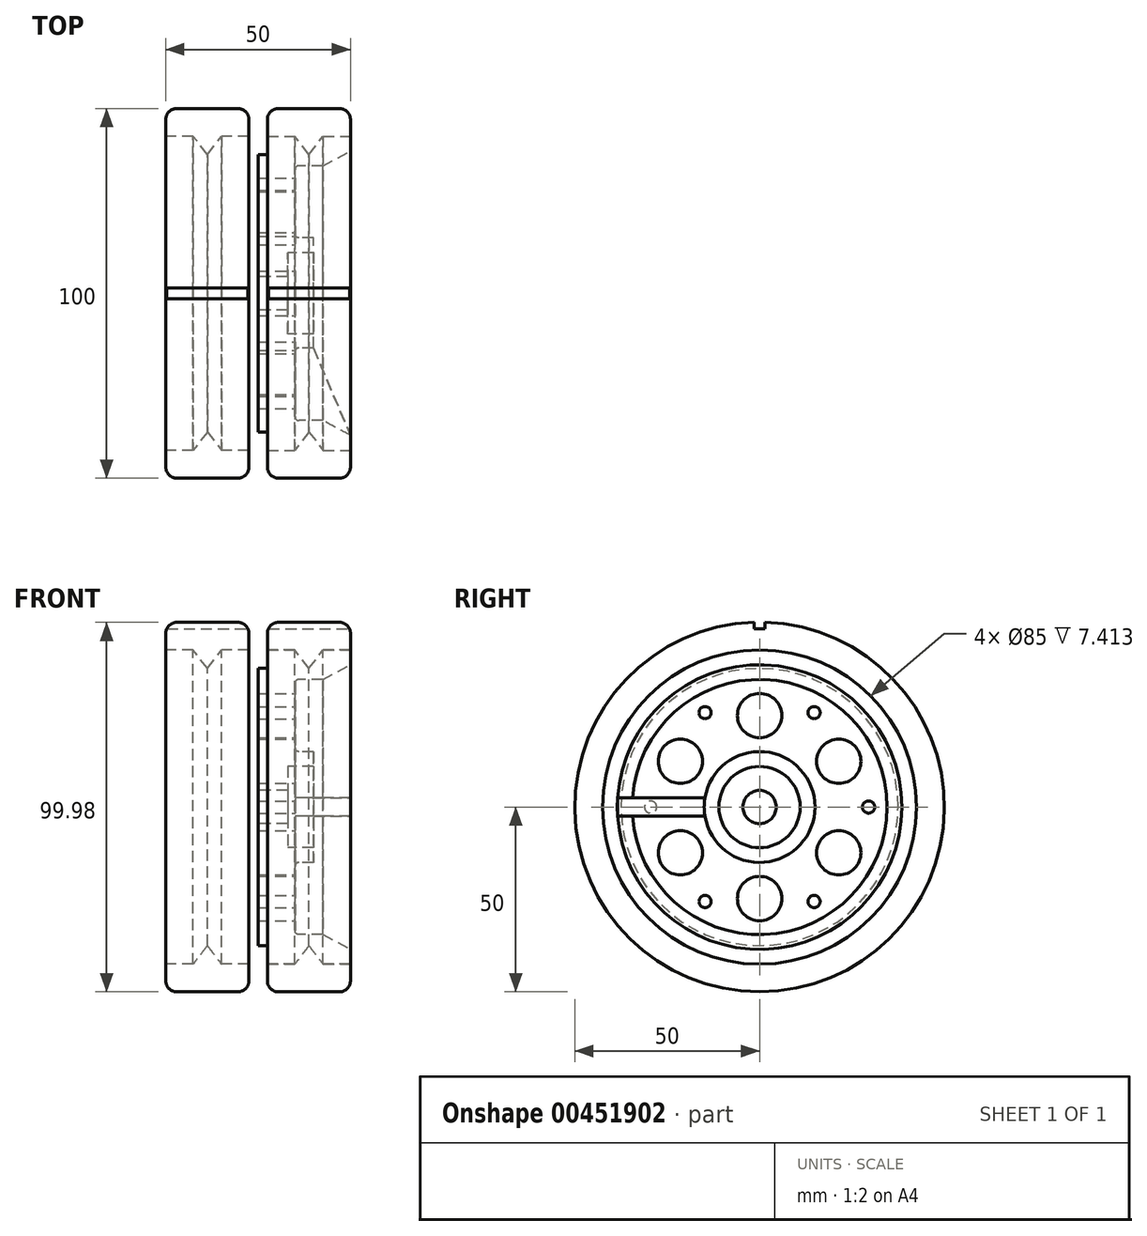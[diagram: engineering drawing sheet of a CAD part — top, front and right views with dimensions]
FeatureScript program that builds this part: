
annotation { "Feature Type Name" : "Feature", "Feature Type Description" : "" }
export const myFeature = defineFeature(function(context is Context, id is Id, definition is map)
    precondition{}
    {
        {
            var Q0;
            Q0=qCreatedBy(makeId("Front.planeOp"),FACE);
            var sketch = newSketch(context, id + "F0", { "sketchPlane" : qUnion([Q0])});
            skLineSegment(sketch, "E0", {"start": v(0, -9.53) * mm, "end": v(0, 22.6) * mm, "construction": true});
            skLineSegment(sketch, "E1", {"start": v(0, 4.5) * mm, "end": v(8, 4.5) * mm});
            skLineSegment(sketch, "E2", {"start": v(8, 4.5) * mm, "end": v(8, 11) * mm});
            skLineSegment(sketch, "E3", {"start": v(8, 11) * mm, "end": v(15, 11) * mm});
            skLineSegment(sketch, "E4", {"start": v(15, 11) * mm, "end": v(15, 15) * mm});
            skLineSegment(sketch, "E5", {"start": v(15, 15) * mm, "end": v(10, 15) * mm});
            skLineSegment(sketch, "E6", {"start": v(10, 15) * mm, "end": v(10, 34.5) * mm});
            skLineSegment(sketch, "E7", {"start": v(10, 34.5) * mm, "end": v(17.5, 34.5) * mm});
            skLineSegment(sketch, "E8", {"start": v(25, 38.5) * mm, "end": v(25, 42.5) * mm});
            skLineSegment(sketch, "E9", {"start": v(25, 42.5) * mm, "end": v(2.5, 42.5) * mm});
            skLineSegment(sketch, "E10", {"start": v(2.5, 42.5) * mm, "end": v(2.5, 37.5) * mm});
            skLineSegment(sketch, "E11", {"start": v(2.5, 37.5) * mm, "end": v(0, 37.5) * mm});
            skLineSegment(sketch, "E12", {"start": v(0, 37.5) * mm, "end": v(0, 4.5) * mm});
            skLineSegment(sketch, "E13", {"start": v(-18.36, 0) * mm, "end": v(12.99, 0) * mm, "construction": true});
            skLineSegment(sketch, "E14", {"start": v(17.5, 34.5) * mm, "end": v(25, 38.5) * mm});
            skPoint(sketch, "E15.orphan", {"position": v(25, 34.5) * mm});
            skSolve(sketch);
        }
        {
            var Q0;
            Q0=makeQuery(id+"FmgyBypNyxviDE3_0.1.F0.imprint","IMPRINT",FACE,{"disambiguationData":[TD([[makeQuery(id+"FmgyBypNyxviDE3_0.1.F0.imprint","IMPRINT",EDGE,{"derivedFrom":sQuery(id+"FmgyBypNyxviDE3_0.1.F0.wireOp",EDGE,"E1")}),1.0]])]});
            var Q1;
            Q1=makeQuery(id+"F0.imprint","IMPRINT",FACE,{"disambiguationData":[TD([[makeQuery(id+"F0.imprint","IMPRINT",EDGE,{"derivedFrom":sQuery(id+"F0.wireOp",EDGE,"E1")}),1.0]])]});
            var Q2;
            Q2=sQuery(id+"F0.wireOp",EDGE,"E13");
            revolve(context, id + "F1", {"entities" : qUnion([Q0, Q1]), "axis" : qUnion([Q2]), "revolveType" : RevolveType.FULL});
        }
        {
            var Q0;
            Q0=qCreatedBy(makeId("Front.planeOp"),FACE);
            var sketch = newSketch(context, id + "F2", { "sketchPlane" : qUnion([Q0])});
            skLineSegment(sketch, "E16", {"start": v(2.5, 42.5) * mm, "end": v(2.5, 47) * mm});
            skLineSegment(sketch, "E17", {"start": v(2.5, 42.5) * mm, "end": v(9.91, 42.5) * mm});
            skLineSegment(sketch, "E18", {"start": v(9.91, 42.5) * mm, "end": v(13.75, 37.5) * mm});
            skLineSegment(sketch, "E19", {"start": v(13.75, 37.5) * mm, "end": v(17.59, 42.5) * mm});
            skLineSegment(sketch, "E20", {"start": v(17.59, 42.5) * mm, "end": v(25, 42.5) * mm});
            skLineSegment(sketch, "E21", {"start": v(25, 42.5) * mm, "end": v(25, 47) * mm});
            skArc(sketch, "E22", {"start": v(2.5, 47) * mm, "mid": v(3.38, 49.12) * mm, "end": v(5.5, 50) * mm});
            skArc(sketch, "E23", {"start": v(25, 47) * mm, "mid": v(24.12, 49.12) * mm, "end": v(22, 50) * mm});
            skLineSegment(sketch, "E24", {"start": v(5.5, 50) * mm, "end": v(22, 50) * mm});
            skLineSegment(sketch, "E25", {"start": v(13.75, 37.5) * mm, "end": v(13.75, 42.5) * mm, "construction": true});
            skSolve(sketch);
        }
        {
            var Q0;
            Q0=makeQuery(id+"F2.imprint","IMPRINT",FACE,{"disambiguationData":[TD([[makeQuery(id+"F2.imprint","IMPRINT",EDGE,{"derivedFrom":sQuery(id+"F2.wireOp",EDGE,"E16")}),-1.0]])]});
            var Q1;
            Q1=makeQuery(id+"F1.opRevolve","SWEPT_EDGE",EDGE,{"disambiguationData":[OSD([sQuery(id+"F0.wireOp",EDGE,"E3"),sQuery(id+"F0.wireOp",EDGE,"E4")])]});
            revolve(context, id + "F3", {"entities" : qUnion([Q0]), "axis" : qUnion([Q1]), "revolveType" : RevolveType.FULL});
        }
        {
            var Q0;
            Q0=makeQuery(id+"F3.opRevolve","SWEPT_BODY",BODY,{"disambiguationData":[OSD([sQuery(id+"F2.wireOp",EDGE,"E16"),sQuery(id+"F2.wireOp",EDGE,"E17"),sQuery(id+"F2.wireOp",EDGE,"E18"),sQuery(id+"F2.wireOp",EDGE,"E19"),sQuery(id+"F2.wireOp",EDGE,"E20"),sQuery(id+"F2.wireOp",EDGE,"E21"),sQuery(id+"F2.wireOp",EDGE,"E22"),sQuery(id+"F2.wireOp",EDGE,"E23"),sQuery(id+"F2.wireOp",EDGE,"E24")])]});
            var Q1;
            Q1=qCreatedBy(makeId("Right.planeOp"),FACE);
            mirror(context, id + "F4", {"entities" : qUnion([Q0]), "mirrorPlane" : qUnion([Q1])});
        }
        {
            var Q0;
            Q0=makeQuery(id+"F1.opRevolve","SWEPT_FACE",FACE,{"disambiguationData":[OSD([sQuery(id+"F0.wireOp",EDGE,"E6")])]});
            var sketch = newSketch(context, id + "F5", { "sketchPlane" : qUnion([Q0])});
            skCircle(sketch, "E26", {"center": v(0, 0) * mm, "radius": 24.75 * mm, "construction": true});
            skCircle(sketch, "E27", {"center": v(0, 24.75) * mm, "radius": 6 * mm});
            skLineSegment(sketch, "E28", {"start": v(-15, 0) * mm, "end": v(-34.5, 0) * mm, "construction": true});
            skPoint(sketch, "E29", {"position": v(-24.75, 0) * mm});
            skCircle(sketch, "E30.1.0", {"center": v(-21.43, 12.38) * mm, "radius": 6 * mm});
            skCircle(sketch, "E30.2.0", {"center": v(-21.43, -12.37) * mm, "radius": 6 * mm});
            skCircle(sketch, "E30.3.0", {"center": v(0, -24.75) * mm, "radius": 6 * mm});
            skCircle(sketch, "E30.4.0", {"center": v(21.43, -12.38) * mm, "radius": 6 * mm});
            skCircle(sketch, "E30.5.0", {"center": v(21.43, 12.38) * mm, "radius": 6 * mm});
            skLineSegment(sketch, "E31", {"start": v(0, 0) * mm, "end": v(-12.38, -21.43) * mm, "construction": true});
            skLineSegment(sketch, "E32", {"start": v(0, 0) * mm, "end": v(12.38, -21.43) * mm, "construction": true});
            skLineSegment(sketch, "E33", {"start": v(0, 0) * mm, "end": v(12.38, 21.43) * mm, "construction": true});
            skLineSegment(sketch, "E34", {"start": v(0, 0) * mm, "end": v(-12.38, 21.43) * mm, "construction": true});
            skPoint(sketch, "E35", {"position": v(-14.75, -25.55) * mm});
            skPoint(sketch, "E36", {"position": v(14.75, -25.55) * mm});
            skPoint(sketch, "E37", {"position": v(29.5, 0) * mm});
            skPoint(sketch, "E38", {"position": v(14.75, 25.55) * mm});
            skPoint(sketch, "E39", {"position": v(-14.75, 25.55) * mm});
            skPoint(sketch, "E40", {"position": v(-29.5, 0) * mm});
            skCircle(sketch, "E41", {"center": v(0, 0) * mm, "radius": 29.5 * mm, "construction": true});
            skSolve(sketch);
        }
        {
            var Q0;
            Q0 = qSketchRegion(id + "F5", true);
            extrude(context, id + "F6", {"entities" : qUnion([Q0]), "operationType" : NewBodyOperationType.REMOVE, "oppositeDirection" : true, "depth" : 25 * mm, "offsetDistance" : 25 * mm});
        }
        {
            var Q0;
            Q0=sQuery(id+"F5.wireOp",VERTEX,"E40");
            var Q1;
            Q1=sQuery(id+"F5.wireOp",VERTEX,"E39");
            var Q2;
            Q2=sQuery(id+"F5.wireOp",VERTEX,"E38");
            var Q3;
            Q3=sQuery(id+"F5.wireOp",VERTEX,"E37");
            var Q4;
            Q4=sQuery(id+"F5.wireOp",VERTEX,"E36");
            var Q5;
            Q5=sQuery(id+"F5.wireOp",VERTEX,"E35");
            var Q6;
            Q6=makeQuery(id+"F1.opRevolve","SWEPT_BODY",BODY,{"disambiguationData":[OSD([sQuery(id+"F0.wireOp",EDGE,"E1"),sQuery(id+"F0.wireOp",EDGE,"E2"),sQuery(id+"F0.wireOp",EDGE,"E3"),sQuery(id+"F0.wireOp",EDGE,"E4"),sQuery(id+"F0.wireOp",EDGE,"E5"),sQuery(id+"F0.wireOp",EDGE,"E6"),sQuery(id+"F0.wireOp",EDGE,"E7"),sQuery(id+"F0.wireOp",EDGE,"E8"),sQuery(id+"F0.wireOp",EDGE,"E9"),sQuery(id+"F0.wireOp",EDGE,"E10"),sQuery(id+"F0.wireOp",EDGE,"E11"),sQuery(id+"F0.wireOp",EDGE,"E12"),sQuery(id+"F0.wireOp",EDGE,"E14")])]});
            var Q7;
            Q7=makeQuery(id+"F1.opRevolve","SWEPT_BODY",BODY,{"disambiguationData":[OSD([sQuery(id+"FmgyBypNyxviDE3_0.1.F0.wireOp",EDGE,"E1"),sQuery(id+"FmgyBypNyxviDE3_0.1.F0.wireOp",EDGE,"E2"),sQuery(id+"FmgyBypNyxviDE3_0.1.F0.wireOp",EDGE,"E3"),sQuery(id+"FmgyBypNyxviDE3_0.1.F0.wireOp",EDGE,"E4"),sQuery(id+"FmgyBypNyxviDE3_0.1.F0.wireOp",EDGE,"E5"),sQuery(id+"FmgyBypNyxviDE3_0.1.F0.wireOp",EDGE,"E6"),sQuery(id+"FmgyBypNyxviDE3_0.1.F0.wireOp",EDGE,"E7"),sQuery(id+"FmgyBypNyxviDE3_0.1.F0.wireOp",EDGE,"E8"),sQuery(id+"FmgyBypNyxviDE3_0.1.F0.wireOp",EDGE,"E9"),sQuery(id+"FmgyBypNyxviDE3_0.1.F0.wireOp",EDGE,"E10"),sQuery(id+"FmgyBypNyxviDE3_0.1.F0.wireOp",EDGE,"E11"),sQuery(id+"FmgyBypNyxviDE3_0.1.F0.wireOp",EDGE,"E12"),sQuery(id+"FmgyBypNyxviDE3_0.1.F0.wireOp",EDGE,"E14")])]});
            hole(context, id + "F7", {"style" : HoleStyle.SIMPLE, "endStyle" : HoleEndStyle.THROUGH, "standardTappedOrClearance" : lookupTablePath({ "standard" : "ISO", "fit" : "Normal", "size" : "M3", "type" : "Clearance" }), "standardBlindInLast" : lookupTablePath({ "fit" : "Standard", "standard" : "ISO", "size" : "M3", "type" : "Clearance" }), "holeDiameter" : 3.3 * mm, "tappedDepth" : 12 * mm, "tapClearance" : 3, "locations" : qUnion([Q0, Q1, Q2, Q3, Q4, Q5]), "scope" : qUnion([Q6, Q7])});
        }
        {
            var Q0;
            Q0=qCreatedBy(makeId("Right.planeOp"),FACE);
            var sketch = newSketch(context, id + "F8", { "sketchPlane" : qUnion([Q0])});
            skLineSegment(sketch, "E42.bottom", {"start": v(1.5, 48.25) * mm, "end": v(-1.5, 48.25) * mm});
            skLineSegment(sketch, "E42.top", {"start": v(1.5, 51.75) * mm, "end": v(-1.5, 51.75) * mm});
            skLineSegment(sketch, "E42.left", {"start": v(1.5, 48.25) * mm, "end": v(1.5, 51.75) * mm});
            skLineSegment(sketch, "E42.right", {"start": v(-1.5, 48.25) * mm, "end": v(-1.5, 51.75) * mm});
            skPoint(sketch, "E42.middle", {"position": v(0, 50) * mm});
            skCircle(sketch, "E43.0", {"center": v(0, 0) * mm, "radius": 50 * mm, "construction": true});
            skSolve(sketch);
        }
        {
            var Q0;
            Q0 = qSketchRegion(id + "F8", true);
            extrude(context, id + "F9", {"entities" : qUnion([Q0]), "operationType" : NewBodyOperationType.REMOVE, "endBound" : BoundingType.SYMMETRIC, "oppositeDirection" : true, "depth" : 100 * mm, "offsetDistance" : 25 * mm});
        }
        {
            var Q0;
            Q0=makeQuery(id+"F1.opRevolve","SWEPT_FACE",FACE,{"disambiguationData":[OSD([sQuery(id+"F0.wireOp",EDGE,"E4")])]});
            var sketch = newSketch(context, id + "F10", { "sketchPlane" : qUnion([Q0])});
            skArc(sketch, "E44", {"start": v(-14.8, 2.5) * mm, "mid": v(-15, 0) * mm, "end": v(-14.8, -2.5) * mm});
            skArc(sketch, "E45", {"start": v(-14.8, -2.5) * mm, "mid": v(15, 0) * mm, "end": v(-14.8, 2.5) * mm});
            skSolve(sketch);
        }
        {
            var Q0;
            Q0=qCreatedBy(makeId("Top.planeOp"),FACE);
            var Q1;
            Q1=sQuery(id+"F10.wireOp",VERTEX,"E44.start");
            cPlane(context, id + "F11", {"entities" : qUnion([Q0, Q1]), "cplaneType" : CPlaneType.PLANE_POINT, "offset" : 25 * mm, "width" : 150 * mm, "height" : 150 * mm});
        }
        {
            var Q0;
            Q0=qCreatedBy(id+"F11.planeOp",FACE);
            var sketch = newSketch(context, id + "F12", { "sketchPlane" : qUnion([Q0])});
            skLineSegment(sketch, "E46", {"start": v(15, -14.8) * mm, "end": v(10, -14.8) * mm});
            skLineSegment(sketch, "E47", {"start": v(10, -14.8) * mm, "end": v(10, -34.4) * mm});
            skLineSegment(sketch, "E48", {"start": v(25, -38.42) * mm, "end": v(15, -14.8) * mm});
            skLineSegment(sketch, "E49", {"start": v(10, -34.4) * mm, "end": v(25, -38.42) * mm});
            skSolve(sketch);
        }
        {
            var Q0;
            Q0=makeQuery(id+"F12.imprint","IMPRINT",FACE,{"disambiguationData":[TD([[makeQuery(id+"F12.imprint","IMPRINT",EDGE,{"derivedFrom":sQuery(id+"F12.wireOp",EDGE,"E46")}),1.0]])]});
            var Q1;
            Q1=sQuery(id+"F10.wireOp",EDGE,"E44");
            sweep(context, id + "F13", {"operationType" : NewBodyOperationType.ADD, "profiles" : qUnion([Q0]), "path" : qUnion([Q1]), "keepProfileOrientation" : true});
        }
        {
            var Q0;
            Q0=makeQuery(id+"F1.opRevolve","SWEPT_EDGE",EDGE,{"disambiguationData":[OSD([sQuery(id+"F0.wireOp",EDGE,"E6"),sQuery(id+"F0.wireOp",EDGE,"E7")])]});
            var Q1;
            Q1=makeQuery(id+"F1.opRevolve","SWEPT_EDGE",EDGE,{"disambiguationData":[OSD([sQuery(id+"FmgyBypNyxviDE3_0.1.F0.wireOp",EDGE,"E6"),sQuery(id+"FmgyBypNyxviDE3_0.1.F0.wireOp",EDGE,"E7")])]});
            var Q2;
            {var subQ0=sQuery(id+"FmgyBypNyxviDE3_0.1.F0.wireOp",EDGE,"E5");var subQ2=sQuery(id+"FmgyBypNyxviDE3_0.1.F0.wireOp",EDGE,"E6");var subQ4=sQuery(id+"F12.wireOp",EDGE,"E48");var subQ5=sQuery(id+"F12.wireOp",EDGE,"E47");var subQ6=sQuery(id+"F12.wireOp",EDGE,"E46");var subQ7=makeQuery(id+"FEM153JQDZezefJ_4.1.F2I4MMrCVyspTrr_4.1.F13.opSweep","CAP_FACE",FACE,{"disambiguationData":[OSD([sQuery(id+"F10.wireOp",VERTEX,"E44.start"),subQ6,subQ5,subQ4])],"isStart":true});var subQ8=sQuery(id+"F10.wireOp",VERTEX,"E44.end");Q2=makeQuery(id+"FEM153JQDZezefJ_4.1.F2I4MMrCVyspTrr_4.2.F13.boolean.opBoolean","SPLIT",EDGE,{"disambiguationData":[TD([subQ7])],"derivedFrom":makeQuery(id+"FEM153JQDZezefJ_4.1.F2I4MMrCVyspTrr_4.1.F13.boolean.opBoolean","SPLIT",EDGE,{"disambiguationData":[TD([makeQuery(id+"FEM153JQDZezefJ_4.1.F13.opSweep","CAP_FACE",FACE,{"disambiguationData":[OSD([subQ8,subQ6,subQ5,subQ4])],"isStart":false})])],"derivedFrom":makeQuery(id+"F1.opRevolve","SWEPT_EDGE",EDGE,{"disambiguationData":[OSD([subQ0,subQ2])]})})});}
            var Q3;
            {var subQ0=sQuery(id+"FmgyBypNyxviDE3_0.1.F0.wireOp",EDGE,"E5");var subQ2=sQuery(id+"FmgyBypNyxviDE3_0.1.F0.wireOp",EDGE,"E6");var subQ4=sQuery(id+"F12.wireOp",EDGE,"E48");var subQ5=sQuery(id+"F12.wireOp",EDGE,"E47");var subQ6=sQuery(id+"F12.wireOp",EDGE,"E46");var subQ7=sQuery(id+"F10.wireOp",VERTEX,"E44.end");var subQ8=sQuery(id+"F10.wireOp",VERTEX,"E44.start");var subQ9=makeQuery(id+"FEM153JQDZezefJ_4.1.F2I4MMrCVyspTrr_4.2.F13.opSweep","CAP_FACE",FACE,{"disambiguationData":[OSD([subQ8,subQ6,subQ5,subQ4])],"isStart":true});var subQ10=makeQuery(id+"FEM153JQDZezefJ_4.1.F13.opSweep","CAP_FACE",FACE,{"disambiguationData":[OSD([subQ7,subQ6,subQ5,subQ4])],"isStart":false});Q3=makeQuery(id+"FEM153JQDZezefJ_4.1.F2I4MMrCVyspTrr_4.3.F13.boolean.opBoolean","SPLIT",EDGE,{"disambiguationData":[TD([subQ9])],"derivedFrom":makeQuery(id+"FEM153JQDZezefJ_4.1.F2I4MMrCVyspTrr_4.2.F13.boolean.opBoolean","SPLIT",EDGE,{"disambiguationData":[TD([subQ10])],"derivedFrom":makeQuery(id+"FEM153JQDZezefJ_4.1.F2I4MMrCVyspTrr_4.1.F13.boolean.opBoolean","SPLIT",EDGE,{"disambiguationData":[TD([subQ10])],"derivedFrom":makeQuery(id+"F1.opRevolve","SWEPT_EDGE",EDGE,{"disambiguationData":[OSD([subQ0,subQ2])]})})})});}
            var Q4;
            {var subQ0=sQuery(id+"FmgyBypNyxviDE3_0.1.F0.wireOp",EDGE,"E5");var subQ2=sQuery(id+"F12.wireOp",EDGE,"E48");var subQ3=sQuery(id+"F12.wireOp",EDGE,"E47");var subQ4=sQuery(id+"F12.wireOp",EDGE,"E46");var subQ5=sQuery(id+"F10.wireOp",VERTEX,"E44.start");var subQ6=makeQuery(id+"FEM153JQDZezefJ_4.1.F2I4MMrCVyspTrr_4.3.F13.opSweep","CAP_FACE",FACE,{"disambiguationData":[OSD([subQ5,subQ4,subQ3,subQ2])],"isStart":true});var subQ7=sQuery(id+"FmgyBypNyxviDE3_0.1.F0.wireOp",EDGE,"E6");var subQ9=sQuery(id+"F10.wireOp",VERTEX,"E44.end");var subQ10=makeQuery(id+"FEM153JQDZezefJ_4.1.F13.opSweep","CAP_FACE",FACE,{"disambiguationData":[OSD([subQ9,subQ4,subQ3,subQ2])],"isStart":false});Q4=makeQuery(id+"FEM153JQDZezefJ_4.1.F2I4MMrCVyspTrr_4.4.F13.boolean.opBoolean","SPLIT",EDGE,{"disambiguationData":[TD([subQ6])],"derivedFrom":makeQuery(id+"FEM153JQDZezefJ_4.1.F2I4MMrCVyspTrr_4.3.F13.boolean.opBoolean","SPLIT",EDGE,{"disambiguationData":[TD([subQ10])],"derivedFrom":makeQuery(id+"FEM153JQDZezefJ_4.1.F2I4MMrCVyspTrr_4.2.F13.boolean.opBoolean","SPLIT",EDGE,{"disambiguationData":[TD([subQ10])],"derivedFrom":makeQuery(id+"FEM153JQDZezefJ_4.1.F2I4MMrCVyspTrr_4.1.F13.boolean.opBoolean","SPLIT",EDGE,{"disambiguationData":[TD([subQ10])],"derivedFrom":makeQuery(id+"F1.opRevolve","SWEPT_EDGE",EDGE,{"disambiguationData":[OSD([subQ0,subQ7])]})})})})});}
            var Q5;
            {var subQ0=sQuery(id+"FmgyBypNyxviDE3_0.1.F0.wireOp",EDGE,"E5");var subQ1=sQuery(id+"F12.wireOp",EDGE,"E48");var subQ2=sQuery(id+"F12.wireOp",EDGE,"E47");var subQ3=sQuery(id+"F12.wireOp",EDGE,"E46");var subQ4=sQuery(id+"FmgyBypNyxviDE3_0.1.F0.wireOp",EDGE,"E6");Q5=makeQuery(id+"FEM153JQDZezefJ_4.1.F2I4MMrCVyspTrr_4.1.F13.boolean.opBoolean","SPLIT",EDGE,{"disambiguationData":[TD([makeQuery(id+"FEM153JQDZezefJ_4.1.F13.opSweep","CAP_FACE",FACE,{"disambiguationData":[OSD([sQuery(id+"F10.wireOp",VERTEX,"E44.start"),subQ3,subQ2,subQ1])],"isStart":true})])],"derivedFrom":makeQuery(id+"F1.opRevolve","SWEPT_EDGE",EDGE,{"disambiguationData":[OSD([subQ0,subQ4])]})});}
            var Q6;
            {var subQ0=sQuery(id+"FmgyBypNyxviDE3_0.1.F0.wireOp",EDGE,"E5");var subQ2=sQuery(id+"FmgyBypNyxviDE3_0.1.F0.wireOp",EDGE,"E6");var subQ4=sQuery(id+"F12.wireOp",EDGE,"E48");var subQ5=sQuery(id+"F12.wireOp",EDGE,"E47");var subQ6=sQuery(id+"F12.wireOp",EDGE,"E46");var subQ8=makeQuery(id+"FEM153JQDZezefJ_4.1.F13.opSweep","CAP_FACE",FACE,{"disambiguationData":[OSD([sQuery(id+"F10.wireOp",VERTEX,"E44.end"),subQ6,subQ5,subQ4])],"isStart":false});Q6=makeQuery(id+"FEM153JQDZezefJ_4.1.F2I4MMrCVyspTrr_4.5.F13.boolean.opBoolean","SPLIT",EDGE,{"disambiguationData":[TD([subQ8])],"derivedFrom":makeQuery(id+"FEM153JQDZezefJ_4.1.F2I4MMrCVyspTrr_4.4.F13.boolean.opBoolean","SPLIT",EDGE,{"disambiguationData":[TD([subQ8])],"derivedFrom":makeQuery(id+"FEM153JQDZezefJ_4.1.F2I4MMrCVyspTrr_4.3.F13.boolean.opBoolean","SPLIT",EDGE,{"disambiguationData":[TD([subQ8])],"derivedFrom":makeQuery(id+"FEM153JQDZezefJ_4.1.F2I4MMrCVyspTrr_4.2.F13.boolean.opBoolean","SPLIT",EDGE,{"disambiguationData":[TD([subQ8])],"derivedFrom":makeQuery(id+"FEM153JQDZezefJ_4.1.F2I4MMrCVyspTrr_4.1.F13.boolean.opBoolean","SPLIT",EDGE,{"disambiguationData":[TD([subQ8])],"derivedFrom":makeQuery(id+"F1.opRevolve","SWEPT_EDGE",EDGE,{"disambiguationData":[OSD([subQ0,subQ2])]})})})})})});}
            var Q7;
            {var subQ0=sQuery(id+"FmgyBypNyxviDE3_0.1.F0.wireOp",EDGE,"E5");var subQ2=sQuery(id+"FmgyBypNyxviDE3_0.1.F0.wireOp",EDGE,"E6");var subQ4=sQuery(id+"F12.wireOp",EDGE,"E48");var subQ5=sQuery(id+"F12.wireOp",EDGE,"E47");var subQ6=sQuery(id+"F12.wireOp",EDGE,"E46");var subQ7=sQuery(id+"F10.wireOp",VERTEX,"E44.start");var subQ8=makeQuery(id+"FEM153JQDZezefJ_4.1.F2I4MMrCVyspTrr_4.4.F13.opSweep","CAP_FACE",FACE,{"disambiguationData":[OSD([subQ7,subQ6,subQ5,subQ4])],"isStart":true});var subQ9=sQuery(id+"F10.wireOp",VERTEX,"E44.end");var subQ10=makeQuery(id+"FEM153JQDZezefJ_4.1.F13.opSweep","CAP_FACE",FACE,{"disambiguationData":[OSD([subQ9,subQ6,subQ5,subQ4])],"isStart":false});Q7=makeQuery(id+"FEM153JQDZezefJ_4.1.F2I4MMrCVyspTrr_4.5.F13.boolean.opBoolean","SPLIT",EDGE,{"disambiguationData":[TD([subQ8])],"derivedFrom":makeQuery(id+"FEM153JQDZezefJ_4.1.F2I4MMrCVyspTrr_4.4.F13.boolean.opBoolean","SPLIT",EDGE,{"disambiguationData":[TD([subQ10])],"derivedFrom":makeQuery(id+"FEM153JQDZezefJ_4.1.F2I4MMrCVyspTrr_4.3.F13.boolean.opBoolean","SPLIT",EDGE,{"disambiguationData":[TD([subQ10])],"derivedFrom":makeQuery(id+"FEM153JQDZezefJ_4.1.F2I4MMrCVyspTrr_4.2.F13.boolean.opBoolean","SPLIT",EDGE,{"disambiguationData":[TD([subQ10])],"derivedFrom":makeQuery(id+"FEM153JQDZezefJ_4.1.F2I4MMrCVyspTrr_4.1.F13.boolean.opBoolean","SPLIT",EDGE,{"disambiguationData":[TD([subQ10])],"derivedFrom":makeQuery(id+"F1.opRevolve","SWEPT_EDGE",EDGE,{"disambiguationData":[OSD([subQ0,subQ2])]})})})})})});}
            var Q8;
            {var subQ0=sQuery(id+"F0.wireOp",EDGE,"E5");var subQ2=sQuery(id+"F12.wireOp",EDGE,"E48");var subQ3=sQuery(id+"F12.wireOp",EDGE,"E47");var subQ4=sQuery(id+"F12.wireOp",EDGE,"E46");var subQ5=sQuery(id+"F10.wireOp",VERTEX,"E44.start");var subQ6=makeQuery(id+"F2I4MMrCVyspTrr_4.3.F13.opSweep","CAP_FACE",FACE,{"disambiguationData":[OSD([subQ5,subQ4,subQ3,subQ2])],"isStart":true});var subQ7=sQuery(id+"F0.wireOp",EDGE,"E6");var subQ9=sQuery(id+"F10.wireOp",VERTEX,"E44.end");var subQ10=makeQuery(id+"F13.opSweep","CAP_FACE",FACE,{"disambiguationData":[OSD([subQ9,subQ4,subQ3,subQ2])],"isStart":false});Q8=makeQuery(id+"F2I4MMrCVyspTrr_4.4.F13.boolean.opBoolean","SPLIT",EDGE,{"disambiguationData":[TD([subQ6])],"derivedFrom":makeQuery(id+"F2I4MMrCVyspTrr_4.3.F13.boolean.opBoolean","SPLIT",EDGE,{"disambiguationData":[TD([subQ10])],"derivedFrom":makeQuery(id+"F2I4MMrCVyspTrr_4.2.F13.boolean.opBoolean","SPLIT",EDGE,{"disambiguationData":[TD([subQ10])],"derivedFrom":makeQuery(id+"F2I4MMrCVyspTrr_4.1.F13.boolean.opBoolean","SPLIT",EDGE,{"disambiguationData":[TD([subQ10])],"derivedFrom":makeQuery(id+"F1.opRevolve","SWEPT_EDGE",EDGE,{"disambiguationData":[OSD([subQ0,subQ7])]})})})})});}
            var Q9;
            {var subQ0=sQuery(id+"F0.wireOp",EDGE,"E5");var subQ2=sQuery(id+"F0.wireOp",EDGE,"E6");var subQ4=sQuery(id+"F12.wireOp",EDGE,"E48");var subQ5=sQuery(id+"F12.wireOp",EDGE,"E47");var subQ6=sQuery(id+"F12.wireOp",EDGE,"E46");var subQ7=sQuery(id+"F10.wireOp",VERTEX,"E44.start");var subQ8=makeQuery(id+"F2I4MMrCVyspTrr_4.4.F13.opSweep","CAP_FACE",FACE,{"disambiguationData":[OSD([subQ7,subQ6,subQ5,subQ4])],"isStart":true});var subQ9=sQuery(id+"F10.wireOp",VERTEX,"E44.end");var subQ10=makeQuery(id+"F13.opSweep","CAP_FACE",FACE,{"disambiguationData":[OSD([subQ9,subQ6,subQ5,subQ4])],"isStart":false});Q9=makeQuery(id+"F2I4MMrCVyspTrr_4.5.F13.boolean.opBoolean","SPLIT",EDGE,{"disambiguationData":[TD([subQ8])],"derivedFrom":makeQuery(id+"F2I4MMrCVyspTrr_4.4.F13.boolean.opBoolean","SPLIT",EDGE,{"disambiguationData":[TD([subQ10])],"derivedFrom":makeQuery(id+"F2I4MMrCVyspTrr_4.3.F13.boolean.opBoolean","SPLIT",EDGE,{"disambiguationData":[TD([subQ10])],"derivedFrom":makeQuery(id+"F2I4MMrCVyspTrr_4.2.F13.boolean.opBoolean","SPLIT",EDGE,{"disambiguationData":[TD([subQ10])],"derivedFrom":makeQuery(id+"F2I4MMrCVyspTrr_4.1.F13.boolean.opBoolean","SPLIT",EDGE,{"disambiguationData":[TD([subQ10])],"derivedFrom":makeQuery(id+"F1.opRevolve","SWEPT_EDGE",EDGE,{"disambiguationData":[OSD([subQ0,subQ2])]})})})})})});}
            var Q10;
            {var subQ0=sQuery(id+"F0.wireOp",EDGE,"E5");var subQ2=sQuery(id+"F0.wireOp",EDGE,"E6");var subQ4=sQuery(id+"F12.wireOp",EDGE,"E48");var subQ5=sQuery(id+"F12.wireOp",EDGE,"E47");var subQ6=sQuery(id+"F12.wireOp",EDGE,"E46");var subQ7=sQuery(id+"F10.wireOp",VERTEX,"E44.end");var subQ8=sQuery(id+"F10.wireOp",VERTEX,"E44.start");var subQ9=makeQuery(id+"F2I4MMrCVyspTrr_4.2.F13.opSweep","CAP_FACE",FACE,{"disambiguationData":[OSD([subQ8,subQ6,subQ5,subQ4])],"isStart":true});var subQ10=makeQuery(id+"F13.opSweep","CAP_FACE",FACE,{"disambiguationData":[OSD([subQ7,subQ6,subQ5,subQ4])],"isStart":false});Q10=makeQuery(id+"F2I4MMrCVyspTrr_4.3.F13.boolean.opBoolean","SPLIT",EDGE,{"disambiguationData":[TD([subQ9])],"derivedFrom":makeQuery(id+"F2I4MMrCVyspTrr_4.2.F13.boolean.opBoolean","SPLIT",EDGE,{"disambiguationData":[TD([subQ10])],"derivedFrom":makeQuery(id+"F2I4MMrCVyspTrr_4.1.F13.boolean.opBoolean","SPLIT",EDGE,{"disambiguationData":[TD([subQ10])],"derivedFrom":makeQuery(id+"F1.opRevolve","SWEPT_EDGE",EDGE,{"disambiguationData":[OSD([subQ0,subQ2])]})})})});}
            var Q11;
            {var subQ0=sQuery(id+"F0.wireOp",EDGE,"E5");var subQ2=sQuery(id+"F0.wireOp",EDGE,"E6");var subQ4=sQuery(id+"F12.wireOp",EDGE,"E48");var subQ5=sQuery(id+"F12.wireOp",EDGE,"E47");var subQ6=sQuery(id+"F12.wireOp",EDGE,"E46");var subQ7=makeQuery(id+"F2I4MMrCVyspTrr_4.1.F13.opSweep","CAP_FACE",FACE,{"disambiguationData":[OSD([sQuery(id+"F10.wireOp",VERTEX,"E44.start"),subQ6,subQ5,subQ4])],"isStart":true});var subQ8=sQuery(id+"F10.wireOp",VERTEX,"E44.end");Q11=makeQuery(id+"F2I4MMrCVyspTrr_4.2.F13.boolean.opBoolean","SPLIT",EDGE,{"disambiguationData":[TD([subQ7])],"derivedFrom":makeQuery(id+"F2I4MMrCVyspTrr_4.1.F13.boolean.opBoolean","SPLIT",EDGE,{"disambiguationData":[TD([makeQuery(id+"F13.opSweep","CAP_FACE",FACE,{"disambiguationData":[OSD([subQ8,subQ6,subQ5,subQ4])],"isStart":false})])],"derivedFrom":makeQuery(id+"F1.opRevolve","SWEPT_EDGE",EDGE,{"disambiguationData":[OSD([subQ0,subQ2])]})})});}
            var Q12;
            {var subQ0=sQuery(id+"F0.wireOp",EDGE,"E5");var subQ1=sQuery(id+"F12.wireOp",EDGE,"E48");var subQ2=sQuery(id+"F12.wireOp",EDGE,"E47");var subQ3=sQuery(id+"F12.wireOp",EDGE,"E46");var subQ4=sQuery(id+"F0.wireOp",EDGE,"E6");Q12=makeQuery(id+"F2I4MMrCVyspTrr_4.1.F13.boolean.opBoolean","SPLIT",EDGE,{"disambiguationData":[TD([makeQuery(id+"F13.opSweep","CAP_FACE",FACE,{"disambiguationData":[OSD([sQuery(id+"F10.wireOp",VERTEX,"E44.start"),subQ3,subQ2,subQ1])],"isStart":true})])],"derivedFrom":makeQuery(id+"F1.opRevolve","SWEPT_EDGE",EDGE,{"disambiguationData":[OSD([subQ0,subQ4])]})});}
            var Q13;
            {var subQ0=sQuery(id+"F0.wireOp",EDGE,"E5");var subQ2=sQuery(id+"F0.wireOp",EDGE,"E6");var subQ4=sQuery(id+"F12.wireOp",EDGE,"E48");var subQ5=sQuery(id+"F12.wireOp",EDGE,"E47");var subQ6=sQuery(id+"F12.wireOp",EDGE,"E46");var subQ8=makeQuery(id+"F13.opSweep","CAP_FACE",FACE,{"disambiguationData":[OSD([sQuery(id+"F10.wireOp",VERTEX,"E44.end"),subQ6,subQ5,subQ4])],"isStart":false});Q13=makeQuery(id+"F2I4MMrCVyspTrr_4.5.F13.boolean.opBoolean","SPLIT",EDGE,{"disambiguationData":[TD([subQ8])],"derivedFrom":makeQuery(id+"F2I4MMrCVyspTrr_4.4.F13.boolean.opBoolean","SPLIT",EDGE,{"disambiguationData":[TD([subQ8])],"derivedFrom":makeQuery(id+"F2I4MMrCVyspTrr_4.3.F13.boolean.opBoolean","SPLIT",EDGE,{"disambiguationData":[TD([subQ8])],"derivedFrom":makeQuery(id+"F2I4MMrCVyspTrr_4.2.F13.boolean.opBoolean","SPLIT",EDGE,{"disambiguationData":[TD([subQ8])],"derivedFrom":makeQuery(id+"F2I4MMrCVyspTrr_4.1.F13.boolean.opBoolean","SPLIT",EDGE,{"disambiguationData":[TD([subQ8])],"derivedFrom":makeQuery(id+"F1.opRevolve","SWEPT_EDGE",EDGE,{"disambiguationData":[OSD([subQ0,subQ2])]})})})})})});}
            fillet(context, id + "F14", {"entities" : qUnion([Q0, Q1, Q2, Q3, Q4, Q5, Q6, Q7, Q8, Q9, Q10, Q11, Q12, Q13]), "radius" : 1 * mm, "tangentPropagation" : true, "allowEdgeOverflow" : false});
        }
        {
            var Q0;
            Q0=makeQuery(id+"F3.opRevolve","SWEPT_BODY",BODY,{"disambiguationData":[OSD([sQuery(id+"F2.wireOp",EDGE,"E16"),sQuery(id+"F2.wireOp",EDGE,"E17"),sQuery(id+"F2.wireOp",EDGE,"E18"),sQuery(id+"F2.wireOp",EDGE,"E19"),sQuery(id+"F2.wireOp",EDGE,"E20"),sQuery(id+"F2.wireOp",EDGE,"E21"),sQuery(id+"F2.wireOp",EDGE,"E22"),sQuery(id+"F2.wireOp",EDGE,"E23"),sQuery(id+"F2.wireOp",EDGE,"E24")])]});
            var Q1;
            Q1=makeQuery(id+"F4.opPattern","COPY",BODY,{"derivedFrom":makeQuery(id+"F3.opRevolve","SWEPT_BODY",BODY,{"disambiguationData":[OSD([sQuery(id+"F2.wireOp",EDGE,"E16"),sQuery(id+"F2.wireOp",EDGE,"E17"),sQuery(id+"F2.wireOp",EDGE,"E18"),sQuery(id+"F2.wireOp",EDGE,"E19"),sQuery(id+"F2.wireOp",EDGE,"E20"),sQuery(id+"F2.wireOp",EDGE,"E21"),sQuery(id+"F2.wireOp",EDGE,"E22"),sQuery(id+"F2.wireOp",EDGE,"E23"),sQuery(id+"F2.wireOp",EDGE,"E24")])]}),"instanceName":"1"});
            var Q2;
            Q2=makeQuery(id+"F1.opRevolve","SWEPT_BODY",BODY,{"disambiguationData":[OSD([sQuery(id+"FmgyBypNyxviDE3_0.1.F0.wireOp",EDGE,"E1"),sQuery(id+"FmgyBypNyxviDE3_0.1.F0.wireOp",EDGE,"E2"),sQuery(id+"FmgyBypNyxviDE3_0.1.F0.wireOp",EDGE,"E3"),sQuery(id+"FmgyBypNyxviDE3_0.1.F0.wireOp",EDGE,"E4"),sQuery(id+"FmgyBypNyxviDE3_0.1.F0.wireOp",EDGE,"E5"),sQuery(id+"FmgyBypNyxviDE3_0.1.F0.wireOp",EDGE,"E6"),sQuery(id+"FmgyBypNyxviDE3_0.1.F0.wireOp",EDGE,"E7"),sQuery(id+"FmgyBypNyxviDE3_0.1.F0.wireOp",EDGE,"E8"),sQuery(id+"FmgyBypNyxviDE3_0.1.F0.wireOp",EDGE,"E9"),sQuery(id+"FmgyBypNyxviDE3_0.1.F0.wireOp",EDGE,"E10"),sQuery(id+"FmgyBypNyxviDE3_0.1.F0.wireOp",EDGE,"E11"),sQuery(id+"FmgyBypNyxviDE3_0.1.F0.wireOp",EDGE,"E12"),sQuery(id+"FmgyBypNyxviDE3_0.1.F0.wireOp",EDGE,"E14")])]});
            var Q3;
            Q3=makeQuery(id+"F1.opRevolve","SWEPT_BODY",BODY,{"disambiguationData":[OSD([sQuery(id+"F0.wireOp",EDGE,"E1"),sQuery(id+"F0.wireOp",EDGE,"E2"),sQuery(id+"F0.wireOp",EDGE,"E3"),sQuery(id+"F0.wireOp",EDGE,"E4"),sQuery(id+"F0.wireOp",EDGE,"E5"),sQuery(id+"F0.wireOp",EDGE,"E6"),sQuery(id+"F0.wireOp",EDGE,"E7"),sQuery(id+"F0.wireOp",EDGE,"E8"),sQuery(id+"F0.wireOp",EDGE,"E9"),sQuery(id+"F0.wireOp",EDGE,"E10"),sQuery(id+"F0.wireOp",EDGE,"E11"),sQuery(id+"F0.wireOp",EDGE,"E12"),sQuery(id+"F0.wireOp",EDGE,"E14")])]});
            booleanBodies(context, id + "F15", {"operationType" : BooleanOperationType.SUBTRACTION, "tools" : qUnion([Q0, Q1]), "targets" : qUnion([Q2, Q3]), "keepTools" : true});
        }
    });
